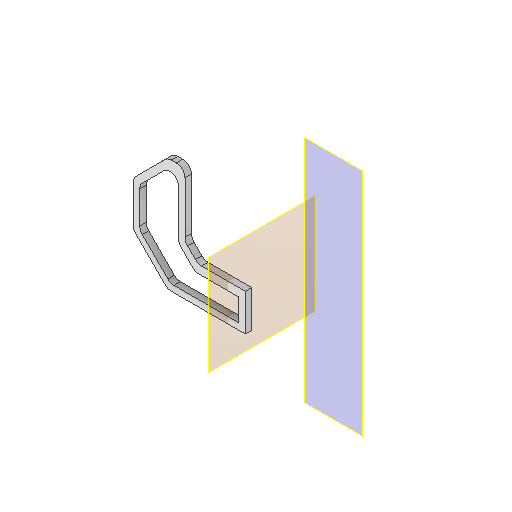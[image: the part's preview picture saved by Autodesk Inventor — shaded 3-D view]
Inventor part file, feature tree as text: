
AUTODESK INVENTOR PART (.ipt)
format: ipt  version: 2022 (Build 260153000, 153)  size: 266,240 bytes
history: native  units: in
note: dims shown in document units (in); Inventor stores cm internally (conversion verified against a paired STEP export)
features: other x11, extrude x7, sketch x7, reference x7, projected_geometry x3, plane x2, fillet x1
ambient origin geometry x8: Origin, YZ Plane, XZ Plane, XY Plane, X Axis, Y Axis, Z Axis, Center Point
bodies: Solid1 (feature_tree)
feature tree (38):
  plane  "Work Plane1"
  extrude  "Extrusion1"  Depth=0.5512in TaperAngle=0.0deg
  extrude  "Extrusion2"  TaperAngle=135.0deg  [1 undecoded]
  extrude  "Extrusion3"  Depth=0.2362in
  extrude  "Extrusion8"  Depth=0.2362in
  extrude  "Extrusion9"  Depth=0.5512in TaperAngle=0.0deg
  plane  "Arbeitsebene3"
  extrude  "Extrusion13"  Depth=0.0591in
  fillet  "Rundung1"  Radius=1.0236in
  extrude  "Extrusion14"  TaperAngle=0.0deg  [1 undecoded]
  sketch  "Sketch1"  dims[d0=0.0591in d1=0.0in d3=0.5512in d4=0.0in]
  sketch  "Sketch2"  dims[d12=0.0591in d13=0.0in d25=135.0deg]
  sketch  "Sketch3"  dims[d26=0.1575in d27=0.2362in]
  reference  "Reference1"
  projected_geometry  "Projected Loop5"
  projected_geometry  "Projected Loop6"
  sketch  "Sketch8"  dims[d28=0.1017in d29=0.2362in]
  reference  "Reference2"
  reference  "Reference3"
  sketch  "Sketch9"  dims[d31=0.4724in d35=0.5512in d36=0.0in]
  reference  "Reference4"
  sketch  "Skizze13"  dims[d40=0.1181in d41=0.0591in d42=1.0236in]
  reference  "Referenz5"
  reference  "Referenz6"
  reference  "Referenz7"
  sketch  "Skizze14"  dims[d43=0.5512in d44=-0.0687in d45=0.0in d50=0.315in d58=0.2559in d60=0.0591in d61=0.0in d62=0.0in d63=0.0591in d64=0.0787in d65=-0.1575in d66=0.1378in d67=0.3937in d68=0.0in]
  projected_geometry  "Projizierte Kontur10"
  other  "Matchboxscope_v1.iam"
  other  "Matchboxscope_sample_v1:1"
  other  "<userpath>\Documents\Matchboxscope\INVENTOR\Matchboxscope_v0.iam"
  other  "Matchboxscope_v0.iam"
  other  "Matchboxscope_sample_v0:1"
  other  "Matchboxscope_middle2_v1:1"
  other  "00_ESP3-CAM:5"
  other  "Bauteil50"
  other  "Matchboxscope_VCM_v1.iam"
  other  "DIN 912 - ersetzt durch DIN EN ISO 4762 M3 x 25:1"
  other  "Matchboxscope_sample_universal:2"
note: 2 required parameter values undecoded (feature->parameter linkage not recoverable at this tier; creation-order binding heuristic only, values carry confidence <= 0.55)
